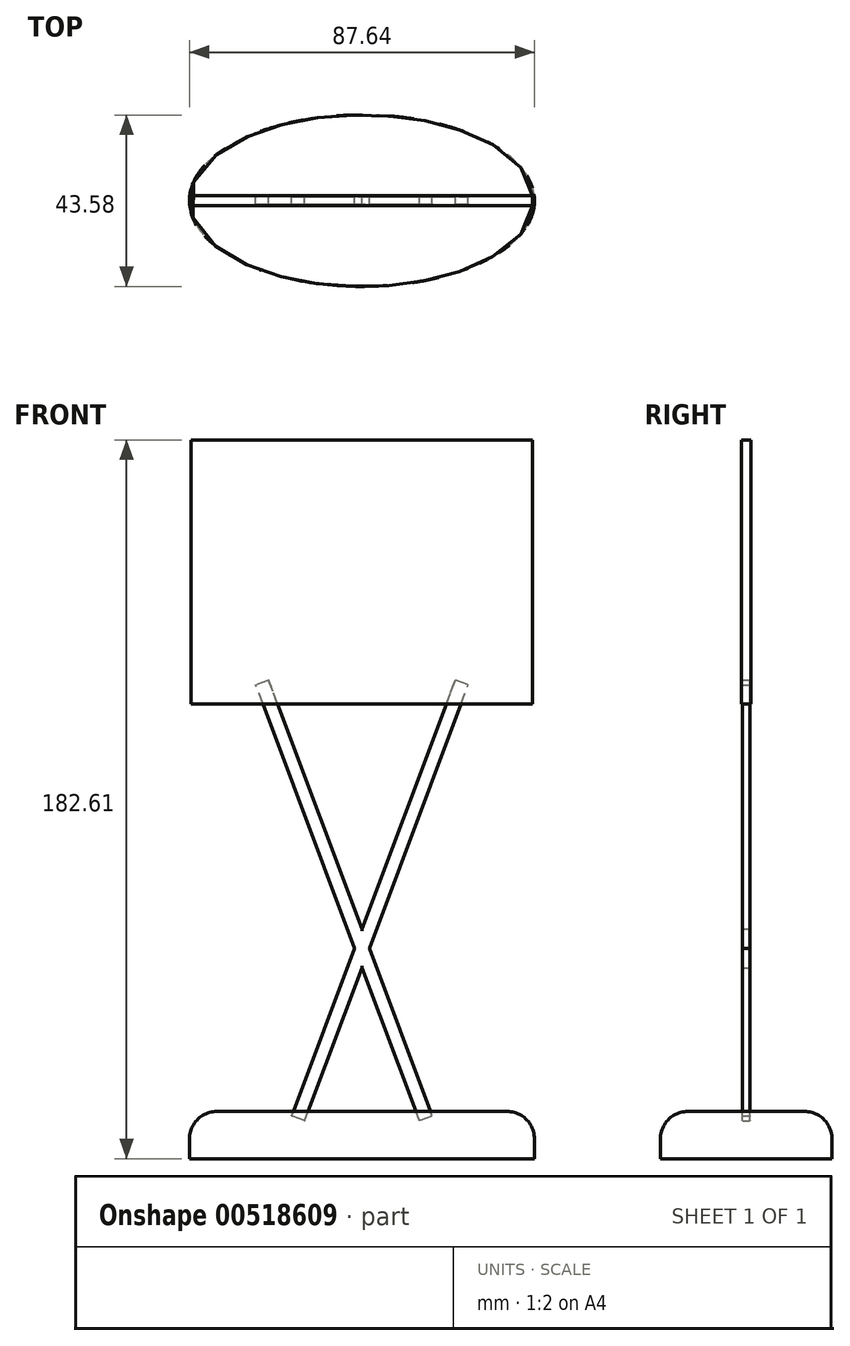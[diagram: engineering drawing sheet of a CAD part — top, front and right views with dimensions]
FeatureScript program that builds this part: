
annotation { "Feature Type Name" : "Feature", "Feature Type Description" : "" }
export const myFeature = defineFeature(function(context is Context, id is Id, definition is map)
    precondition{}
    {
        {
            var Q0;
            Q0=qCreatedBy(makeId("Top.planeOp"),FACE);
            var sketch = newSketch(context, id + "F0", { "sketchPlane" : qUnion([Q0])});
            skEllipse(sketch, "E0", {"center": v(0, 0) * mm, "majorRadius": 43.82 * mm, "minorRadius": 21.79 * mm, "majorAxis": v(1, 0)});
            skSolve(sketch);
        }
        {
            var Q0;
            Q0=qCreatedBy(makeId("Front.planeOp"),FACE);
            var sketch = newSketch(context, id + "F1", { "sketchPlane" : qUnion([Q0])});
            skLineSegment(sketch, "E1.bottom", {"start": v(43.38, 115.48) * mm, "end": v(-43.38, 115.48) * mm});
            skLineSegment(sketch, "E1.top", {"start": v(43.38, 182.6) * mm, "end": v(-43.38, 182.6) * mm});
            skLineSegment(sketch, "E1.left", {"start": v(43.38, 115.48) * mm, "end": v(43.38, 182.6) * mm});
            skLineSegment(sketch, "E1.right", {"start": v(-43.38, 115.48) * mm, "end": v(-43.38, 182.6) * mm});
            skPoint(sketch, "E1.middle", {"position": v(0, 149.04) * mm});
            skSolve(sketch);
        }
        {
            var Q0;
            Q0 = qSketchRegion(id + "F0", true);
            extrude(context, id + "F2", {"entities" : qUnion([Q0]), "depth" : 12 * mm, "offsetDistance" : 25 * mm});
        }
        {
            var Q0;
            Q0 = qSketchRegion(id + "F1", true);
            extrude(context, id + "F3", {"entities" : qUnion([Q0]), "depth" : 1.25 * mm, "offsetDistance" : 25 * mm, "hasSecondDirection" : true, "secondDirectionOppositeDirection" : true, "secondDirectionDepth" : 1.25 * mm});
        }
        {
            var Q0;
            Q0=qCreatedBy(makeId("Front.planeOp"),FACE);
            var sketch = newSketch(context, id + "F4", { "sketchPlane" : qUnion([Q0])});
            skLineSegment(sketch, "E2", {"start": v(-14.56, 9.64) * mm, "end": v(26.98, 120.34) * mm});
            skLineSegment(sketch, "E3.0", {"start": v(-17.83, 10.87) * mm, "end": v(23.7, 121.57) * mm});
            skLineSegment(sketch, "E4", {"start": v(-14.56, 9.64) * mm, "end": v(-17.83, 10.87) * mm});
            skLineSegment(sketch, "E5", {"start": v(26.98, 120.34) * mm, "end": v(23.7, 121.57) * mm});
            skLineSegment(sketch, "E6.MirrorCS", {"start": v(14.56, 9.64) * mm, "end": v(-26.98, 120.34) * mm});
            skLineSegment(sketch, "E7.MirrorCS", {"start": v(17.83, 10.87) * mm, "end": v(-23.7, 121.57) * mm});
            skLineSegment(sketch, "E8", {"start": v(-23.7, 121.57) * mm, "end": v(-26.98, 120.34) * mm});
            skLineSegment(sketch, "E9", {"start": v(17.83, 10.87) * mm, "end": v(14.56, 9.64) * mm});
            skSolve(sketch);
        }
        {
            var Q0;
            Q0 = qSketchRegion(id + "F4", true);
            extrude(context, id + "F5", {"entities" : qUnion([Q0]), "depth" : 1 * mm, "offsetDistance" : 25 * mm, "hasSecondDirection" : true, "secondDirectionOppositeDirection" : true, "secondDirectionDepth" : 1 * mm});
        }
        {
            var Q0;
            Q0=makeQuery(id+"F2.opExtrude","CAP_EDGE",EDGE,{"disambiguationData":[OSD([sQuery(id+"F0.wireOp",EDGE,"E0")])],"isStart":false});
            fillet(context, id + "F6", {"entities" : qUnion([Q0]), "radius" : 7 * mm, "tangentPropagation" : true, "allowEdgeOverflow" : false});
        }
        {
            var Q0;
            {var subQ0=sQuery(id+"F4.wireOp",EDGE,"E7.MirrorCS");Q0=makeQuery(id+"F5.opExtrude","CAP_EDGE",EDGE,{"disambiguationData":[OSD([subQ0]),TDD([makeQuery(id+"F4.imprint","IMPRINT",EDGE,{"disambiguationData":[TD([[makeQuery(id+"F4.imprint","INTERSECT",VERTEX,{"derivedFrom":[subQ0,sQuery(id+"F4.wireOp",EDGE,"E8")]}),1.0]])],"derivedFrom":subQ0})])],"isStart":false});}
            var Q1;
            {var subQ0=sQuery(id+"F4.wireOp",EDGE,"E7.MirrorCS");Q1=makeQuery(id+"F5.opExtrude","CAP_EDGE",EDGE,{"disambiguationData":[OSD([subQ0]),TDD([makeQuery(id+"F4.imprint","IMPRINT",EDGE,{"disambiguationData":[TD([[makeQuery(id+"F4.imprint","INTERSECT",VERTEX,{"derivedFrom":[subQ0,sQuery(id+"F4.wireOp",EDGE,"E8")]}),1.0]])],"derivedFrom":subQ0})])],"isStart":true});}
            var Q2;
            {var subQ0=sQuery(id+"F4.wireOp",EDGE,"E2");Q2=makeQuery(id+"F5.opExtrude","CAP_EDGE",EDGE,{"disambiguationData":[OSD([subQ0]),TDD([makeQuery(id+"F4.imprint","IMPRINT",EDGE,{"disambiguationData":[TD([[makeQuery(id+"F4.imprint","INTERSECT",VERTEX,{"derivedFrom":[subQ0,sQuery(id+"F4.wireOp",EDGE,"E5")]}),1.0]])],"derivedFrom":subQ0})])],"isStart":false});}
            var Q3;
            {var subQ0=sQuery(id+"F4.wireOp",EDGE,"E3.0");Q3=makeQuery(id+"F5.opExtrude","CAP_EDGE",EDGE,{"disambiguationData":[OSD([subQ0]),TDD([makeQuery(id+"F4.imprint","IMPRINT",EDGE,{"disambiguationData":[TD([[makeQuery(id+"F4.imprint","INTERSECT",VERTEX,{"derivedFrom":[subQ0,sQuery(id+"F4.wireOp",EDGE,"E5")]}),1.0]])],"derivedFrom":subQ0})])],"isStart":false});}
            var Q4;
            {var subQ0=sQuery(id+"F4.wireOp",EDGE,"E2");Q4=makeQuery(id+"F5.opExtrude","CAP_EDGE",EDGE,{"disambiguationData":[OSD([subQ0]),TDD([makeQuery(id+"F4.imprint","IMPRINT",EDGE,{"disambiguationData":[TD([[makeQuery(id+"F4.imprint","INTERSECT",VERTEX,{"derivedFrom":[subQ0,sQuery(id+"F4.wireOp",EDGE,"E5")]}),1.0]])],"derivedFrom":subQ0})])],"isStart":true});}
            var Q5;
            {var subQ0=sQuery(id+"F4.wireOp",EDGE,"E7.MirrorCS");Q5=makeQuery(id+"F5.opExtrude","CAP_EDGE",EDGE,{"disambiguationData":[OSD([subQ0]),TDD([makeQuery(id+"F4.imprint","IMPRINT",EDGE,{"disambiguationData":[TD([[makeQuery(id+"F4.imprint","INTERSECT",VERTEX,{"derivedFrom":[subQ0,sQuery(id+"F4.wireOp",EDGE,"E9")]}),-1.0]])],"derivedFrom":subQ0})])],"isStart":false});}
            var Q6;
            {var subQ0=sQuery(id+"F4.wireOp",EDGE,"E7.MirrorCS");Q6=makeQuery(id+"F5.opExtrude","CAP_EDGE",EDGE,{"disambiguationData":[OSD([subQ0]),TDD([makeQuery(id+"F4.imprint","IMPRINT",EDGE,{"disambiguationData":[TD([[makeQuery(id+"F4.imprint","INTERSECT",VERTEX,{"derivedFrom":[subQ0,sQuery(id+"F4.wireOp",EDGE,"E9")]}),-1.0]])],"derivedFrom":subQ0})])],"isStart":true});}
            var Q7;
            {var subQ0=sQuery(id+"F4.wireOp",EDGE,"E2");Q7=makeQuery(id+"F5.opExtrude","CAP_EDGE",EDGE,{"disambiguationData":[OSD([subQ0]),TDD([makeQuery(id+"F4.imprint","IMPRINT",EDGE,{"disambiguationData":[TD([[makeQuery(id+"F4.imprint","INTERSECT",VERTEX,{"derivedFrom":[subQ0,sQuery(id+"F4.wireOp",EDGE,"E4")]}),-1.0]])],"derivedFrom":subQ0})])],"isStart":false});}
            var Q8;
            {var subQ0=sQuery(id+"F4.wireOp",EDGE,"E2");Q8=makeQuery(id+"F5.opExtrude","CAP_EDGE",EDGE,{"disambiguationData":[OSD([subQ0]),TDD([makeQuery(id+"F4.imprint","IMPRINT",EDGE,{"disambiguationData":[TD([[makeQuery(id+"F4.imprint","INTERSECT",VERTEX,{"derivedFrom":[subQ0,sQuery(id+"F4.wireOp",EDGE,"E4")]}),-1.0]])],"derivedFrom":subQ0})])],"isStart":true});}
            var Q9;
            {var subQ0=sQuery(id+"F4.wireOp",EDGE,"E3.0");Q9=makeQuery(id+"F5.opExtrude","CAP_EDGE",EDGE,{"disambiguationData":[OSD([subQ0]),TDD([makeQuery(id+"F4.imprint","IMPRINT",EDGE,{"disambiguationData":[TD([[makeQuery(id+"F4.imprint","INTERSECT",VERTEX,{"derivedFrom":[subQ0,sQuery(id+"F4.wireOp",EDGE,"E4")]}),-1.0]])],"derivedFrom":subQ0})])],"isStart":false});}
            var Q10;
            {var subQ0=sQuery(id+"F4.wireOp",EDGE,"E6.MirrorCS");Q10=makeQuery(id+"F5.opExtrude","CAP_EDGE",EDGE,{"disambiguationData":[OSD([subQ0]),TDD([makeQuery(id+"F4.imprint","IMPRINT",EDGE,{"disambiguationData":[TD([[makeQuery(id+"F4.imprint","INTERSECT",VERTEX,{"derivedFrom":[subQ0,sQuery(id+"F4.wireOp",EDGE,"E8")]}),1.0]])],"derivedFrom":subQ0})])],"isStart":false});}
            var Q11;
            {var subQ0=sQuery(id+"F4.wireOp",EDGE,"E3.0");Q11=makeQuery(id+"F5.opExtrude","CAP_EDGE",EDGE,{"disambiguationData":[OSD([subQ0]),TDD([makeQuery(id+"F4.imprint","IMPRINT",EDGE,{"disambiguationData":[TD([[makeQuery(id+"F4.imprint","INTERSECT",VERTEX,{"derivedFrom":[subQ0,sQuery(id+"F4.wireOp",EDGE,"E4")]}),-1.0]])],"derivedFrom":subQ0})])],"isStart":true});}
            var Q12;
            {var subQ0=sQuery(id+"F4.wireOp",EDGE,"E6.MirrorCS");Q12=makeQuery(id+"F5.opExtrude","CAP_EDGE",EDGE,{"disambiguationData":[OSD([subQ0]),TDD([makeQuery(id+"F4.imprint","IMPRINT",EDGE,{"disambiguationData":[TD([[makeQuery(id+"F4.imprint","INTERSECT",VERTEX,{"derivedFrom":[subQ0,sQuery(id+"F4.wireOp",EDGE,"E8")]}),1.0]])],"derivedFrom":subQ0})])],"isStart":true});}
            var Q13;
            {var subQ0=sQuery(id+"F4.wireOp",EDGE,"E6.MirrorCS");Q13=makeQuery(id+"F5.opExtrude","CAP_EDGE",EDGE,{"disambiguationData":[OSD([subQ0]),TDD([makeQuery(id+"F4.imprint","IMPRINT",EDGE,{"disambiguationData":[TD([[makeQuery(id+"F4.imprint","INTERSECT",VERTEX,{"derivedFrom":[subQ0,sQuery(id+"F4.wireOp",EDGE,"E9")]}),-1.0]])],"derivedFrom":subQ0})])],"isStart":true});}
            var Q14;
            {var subQ0=sQuery(id+"F4.wireOp",EDGE,"E6.MirrorCS");Q14=makeQuery(id+"F5.opExtrude","CAP_EDGE",EDGE,{"disambiguationData":[OSD([subQ0]),TDD([makeQuery(id+"F4.imprint","IMPRINT",EDGE,{"disambiguationData":[TD([[makeQuery(id+"F4.imprint","INTERSECT",VERTEX,{"derivedFrom":[subQ0,sQuery(id+"F4.wireOp",EDGE,"E9")]}),-1.0]])],"derivedFrom":subQ0})])],"isStart":false});}
            fillet(context, id + "F7", {"entities" : qUnion([Q0, Q1, Q2, Q3, Q4, Q5, Q6, Q7, Q8, Q9, Q10, Q11, Q12, Q13, Q14]), "radius" : 0.2 * mm, "tangentPropagation" : true, "allowEdgeOverflow" : false});
        }
    });
